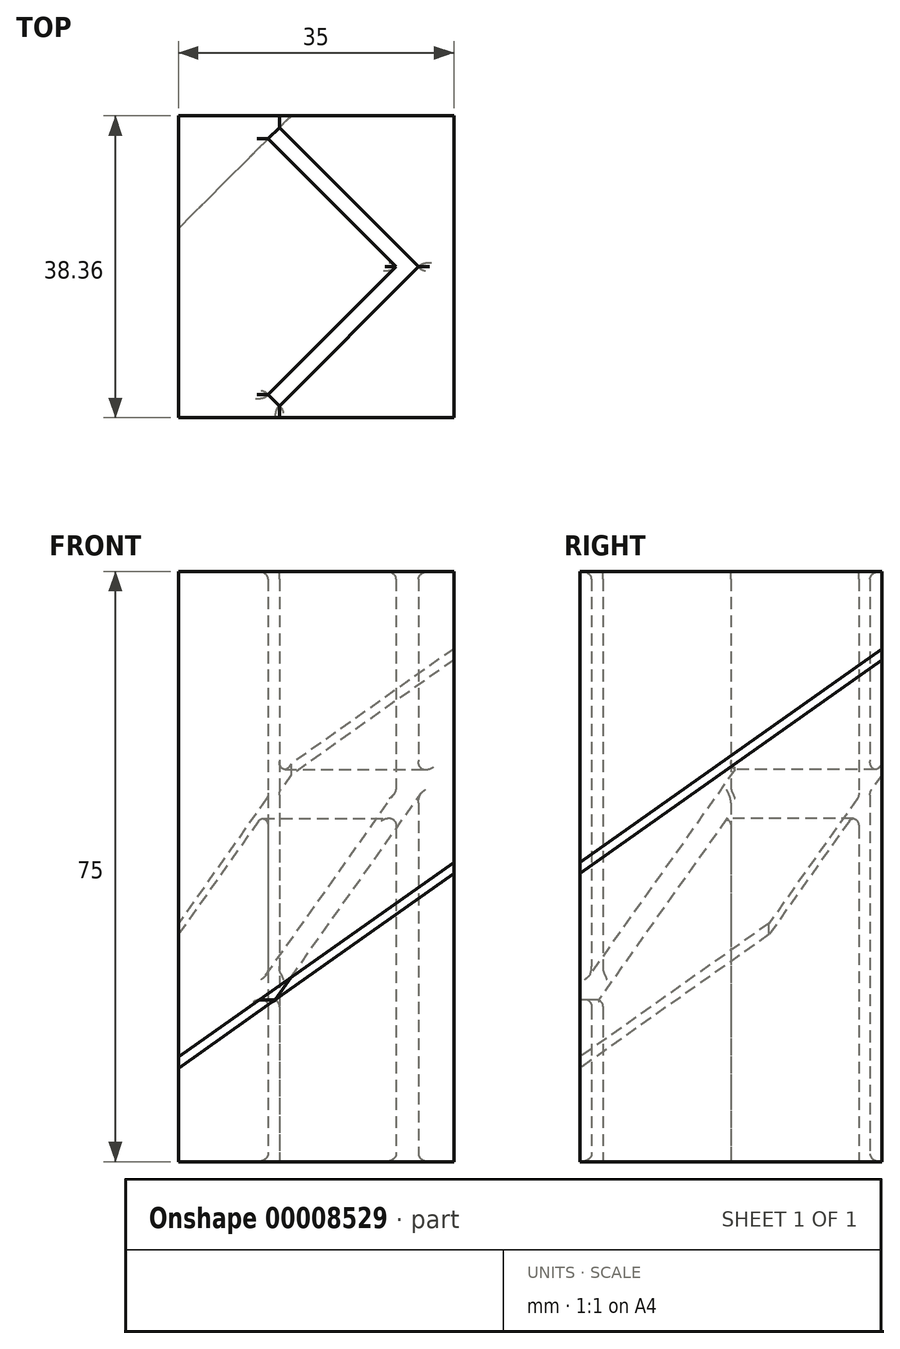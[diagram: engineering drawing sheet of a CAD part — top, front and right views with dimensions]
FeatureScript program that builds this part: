
annotation { "Feature Type Name" : "Feature", "Feature Type Description" : "" }
export const myFeature = defineFeature(function(context is Context, id is Id, definition is map)
    precondition{}
    {
        {
            var Q0;
            Q0=qCreatedBy(makeId("Top.planeOp"),FACE);
            var sketch = newSketch(context, id + "F0", { "sketchPlane" : qUnion([Q0])});
            skLineSegment(sketch, "E0.bottom", {"start": v(-17.5, -19.18) * mm, "end": v(17.5, -19.18) * mm});
            skLineSegment(sketch, "E0.top", {"start": v(-17.5, 19.18) * mm, "end": v(17.5, 19.18) * mm});
            skLineSegment(sketch, "E0.left", {"start": v(-17.5, -19.18) * mm, "end": v(-17.5, 19.18) * mm});
            skLineSegment(sketch, "E0.right", {"start": v(17.5, -19.18) * mm, "end": v(17.5, 19.18) * mm});
            skPoint(sketch, "E0.middle", {"position": v(0, 0) * mm});
            skLineSegment(sketch, "E1.bottom", {"start": v(-22.36, 0) * mm, "end": v(-4.68, -17.68) * mm});
            skLineSegment(sketch, "E1.top", {"start": v(-4.68, 17.68) * mm, "end": v(13, 0) * mm});
            skLineSegment(sketch, "E1.left", {"start": v(-22.36, 0) * mm, "end": v(-4.68, 17.68) * mm});
            skLineSegment(sketch, "E1.right", {"start": v(-4.68, -17.68) * mm, "end": v(13, 0) * mm});
            skLineSegment(sketch, "E2.0", {"start": v(-6.1, -16.26) * mm, "end": v(10.17, 0) * mm});
            skLineSegment(sketch, "E2.1", {"start": v(-6.1, 16.26) * mm, "end": v(10.17, 0) * mm});
            skSolve(sketch);
        }
        {
            var Q0;
            {var subQ9=sQuery(id+"F0.wireOp",EDGE,"E0.bottom");Q0=makeQuery(id+"F0.imprint","IMPRINT",FACE,{"disambiguationData":[TD([[makeQuery(id+"F0.imprint","IMPRINT",EDGE,{"derivedFrom":subQ9}),1.0]])]});}
            var Q1;
            {var subQ0=sQuery(id+"F0.wireOp",EDGE,"E2.0");Q1=makeQuery(id+"F0.imprint","IMPRINT",FACE,{"disambiguationData":[TD([[makeQuery(id+"F0.imprint","IMPRINT",EDGE,{"derivedFrom":subQ0}),1.0]])]});}
            extrude(context, id + "F1", {"entities" : qUnion([Q0, Q1]), "depth" : 75 * mm});
        }
        {
            var Q0;
            Q0=makeQuery(id+"F1.opExtrude","SWEPT_FACE",FACE,{"disambiguationData":[OSD([sQuery(id+"F0.wireOp",EDGE,"E2.0")])]});
            var sketch = newSketch(context, id + "F2", { "sketchPlane" : qUnion([Q0])});
            skLineSegment(sketch, "E3.0.0", {"start": v(-15.8, 0) * mm, "end": v(7.2, 0) * mm});
            skLineSegment(sketch, "E3.0.1", {"start": v(7.2, 0) * mm, "end": v(7.2, 75) * mm});
            skLineSegment(sketch, "E3.0.2", {"start": v(7.2, 75) * mm, "end": v(-15.8, 75) * mm});
            skLineSegment(sketch, "E3.0.3", {"start": v(-15.8, 75) * mm, "end": v(-15.8, 0) * mm});
            skLineSegment(sketch, "E4.0.0", {"start": v(9.2, 0) * mm, "end": v(-15.8, 0) * mm});
            skLineSegment(sketch, "E4.0.1", {"start": v(-15.8, 0) * mm, "end": v(-15.8, 75) * mm});
            skLineSegment(sketch, "E4.0.2", {"start": v(-15.8, 75) * mm, "end": v(9.2, 75) * mm});
            skLineSegment(sketch, "E4.0.3", {"start": v(9.2, 75) * mm, "end": v(9.2, 0) * mm});
            skLineSegment(sketch, "E5", {"start": v(32.72, 70.52) * mm, "end": v(-42.6, -4.8) * mm});
            skLineSegment(sketch, "E6.0", {"start": v(34.67, 73.89) * mm, "end": v(-43.44, -4.23) * mm});
            skLineSegment(sketch, "E7", {"start": v(34.67, 73.89) * mm, "end": v(32.72, 70.52) * mm});
            skLineSegment(sketch, "E8", {"start": v(-42.6, -4.8) * mm, "end": v(-43.44, -4.23) * mm});
            skSolve(sketch);
        }
        {
            var Q0;
            {var subQ0=sQuery(id+"F2.wireOp",EDGE,"E6.0");var subQ1=sQuery(id+"F2.wireOp",EDGE,"E3.0.1");var subQ2=makeQuery(id+"F2.imprint","INTERSECT",VERTEX,{"derivedFrom":[subQ1,subQ0]});Q0=makeQuery(id+"F2.imprint","IMPRINT",FACE,{"disambiguationData":[TD([[makeQuery(id+"F2.imprint","IMPRINT",EDGE,{"disambiguationData":[TD([[subQ2,-1.0]])],"derivedFrom":subQ1}),-1.0]])]});}
            var Q1;
            {var subQ0=sQuery(id+"F2.wireOp",EDGE,"E6.0");var subQ1=sQuery(id+"F2.wireOp",EDGE,"E3.0.1");var subQ2=makeQuery(id+"F2.imprint","INTERSECT",VERTEX,{"derivedFrom":[subQ1,subQ0]});Q1=makeQuery(id+"F2.imprint","IMPRINT",FACE,{"disambiguationData":[TD([[makeQuery(id+"F2.imprint","IMPRINT",EDGE,{"disambiguationData":[TD([[subQ2,-1.0]])],"derivedFrom":subQ1}),1.0]])]});}
            var Q2;
            {var subQ5=sQuery(id+"F2.wireOp",EDGE,"E8");Q2=makeQuery(id+"F2.imprint","IMPRINT",FACE,{"disambiguationData":[TD([[makeQuery(id+"F2.imprint","IMPRINT",EDGE,{"derivedFrom":subQ5}),-1.0]])]});}
            var Q3;
            {var subQ5=sQuery(id+"F2.wireOp",EDGE,"E7");Q3=makeQuery(id+"F2.imprint","IMPRINT",FACE,{"disambiguationData":[TD([[makeQuery(id+"F2.imprint","IMPRINT",EDGE,{"derivedFrom":subQ5}),-1.0]])]});}
            extrude(context, id + "F3", {"entities" : qUnion([Q0, Q1, Q2, Q3]), "operationType" : NewBodyOperationType.REMOVE, "depth" : 46 * mm, "symmetric" : true});
        }
        {
            var Q0;
            Q0=makeQuery(id+"F1.opExtrude","CAP_EDGE",EDGE,{"disambiguationData":[OSD([sQuery(id+"F0.wireOp",EDGE,"E2.0")])],"isStart":false});
            var Q1;
            Q1=makeQuery(id+"F1.opExtrude","CAP_EDGE",EDGE,{"disambiguationData":[OSD([sQuery(id+"F0.wireOp",EDGE,"E2.1")])],"isStart":false});
            var Q2;
            Q2=makeQuery(id+"F1.opExtrude","CAP_EDGE",EDGE,{"disambiguationData":[OSD([sQuery(id+"F0.wireOp",EDGE,"E1.top")])],"isStart":false});
            var Q3;
            Q3=makeQuery(id+"F1.opExtrude","CAP_EDGE",EDGE,{"disambiguationData":[OSD([sQuery(id+"F0.wireOp",EDGE,"E1.right")])],"isStart":false});
            var Q4;
            Q4=makeQuery(id+"F1.opExtrude","CAP_EDGE",EDGE,{"disambiguationData":[OSD([sQuery(id+"F0.wireOp",EDGE,"E1.left")])],"isStart":false});
            var Q5;
            Q5=makeQuery(id+"F1.opExtrude","CAP_EDGE",EDGE,{"disambiguationData":[OSD([sQuery(id+"F0.wireOp",EDGE,"E1.bottom")])],"isStart":false});
            var Q6;
            Q6=makeQuery(id+"F1.opExtrude","CAP_EDGE",EDGE,{"disambiguationData":[OSD([sQuery(id+"F0.wireOp",EDGE,"E1.right")])],"isStart":true});
            var Q7;
            Q7=makeQuery(id+"F1.opExtrude","CAP_EDGE",EDGE,{"disambiguationData":[OSD([sQuery(id+"F0.wireOp",EDGE,"E1.top")])],"isStart":true});
            var Q8;
            Q8=makeQuery(id+"F1.opExtrude","CAP_EDGE",EDGE,{"disambiguationData":[OSD([sQuery(id+"F0.wireOp",EDGE,"E2.1")])],"isStart":true});
            var Q9;
            Q9=makeQuery(id+"F1.opExtrude","CAP_EDGE",EDGE,{"disambiguationData":[OSD([sQuery(id+"F0.wireOp",EDGE,"E2.0")])],"isStart":true});
            var Q10;
            Q10=makeQuery(id+"F1.opExtrude","CAP_EDGE",EDGE,{"disambiguationData":[OSD([sQuery(id+"F0.wireOp",EDGE,"E1.bottom")])],"isStart":true});
            var Q11;
            Q11=makeQuery(id+"F1.opExtrude","CAP_EDGE",EDGE,{"disambiguationData":[OSD([sQuery(id+"F0.wireOp",EDGE,"E1.left")])],"isStart":true});
            var Q12;
            Q12=makeQuery(id+"F3.boolean.opBoolean","INTERSECT",EDGE,{"derivedFrom":[makeQuery(id+"F1.opExtrude","SWEPT_FACE",FACE,{"disambiguationData":[OSD([sQuery(id+"F0.wireOp",EDGE,"E1.top")])]}),makeQuery(id+"F3.opExtrude","SWEPT_FACE",FACE,{"disambiguationData":[OSD([sQuery(id+"F2.wireOp",EDGE,"E5")])]})]});
            var Q13;
            Q13=makeQuery(id+"F3.boolean.opBoolean","INTERSECT",EDGE,{"derivedFrom":[makeQuery(id+"F1.opExtrude","SWEPT_FACE",FACE,{"disambiguationData":[OSD([sQuery(id+"F0.wireOp",EDGE,"E2.1")])]}),makeQuery(id+"F3.opExtrude","SWEPT_FACE",FACE,{"disambiguationData":[OSD([sQuery(id+"F2.wireOp",EDGE,"E5")])]})]});
            var Q14;
            Q14=makeQuery(id+"F3.boolean.opBoolean","INTERSECT",EDGE,{"derivedFrom":[makeQuery(id+"F1.opExtrude","SWEPT_FACE",FACE,{"disambiguationData":[OSD([sQuery(id+"F0.wireOp",EDGE,"E2.0")])]}),makeQuery(id+"F3.opExtrude","SWEPT_FACE",FACE,{"disambiguationData":[OSD([sQuery(id+"F2.wireOp",EDGE,"E5")])]})]});
            var Q15;
            Q15=makeQuery(id+"F3.boolean.opBoolean","INTERSECT",EDGE,{"derivedFrom":[makeQuery(id+"F1.opExtrude","SWEPT_FACE",FACE,{"disambiguationData":[OSD([sQuery(id+"F0.wireOp",EDGE,"E1.right")])]}),makeQuery(id+"F3.opExtrude","SWEPT_FACE",FACE,{"disambiguationData":[OSD([sQuery(id+"F2.wireOp",EDGE,"E5")])]})]});
            var Q16;
            Q16=makeQuery(id+"F3.boolean.opBoolean","INTERSECT",EDGE,{"derivedFrom":[makeQuery(id+"F1.opExtrude","SWEPT_FACE",FACE,{"disambiguationData":[OSD([sQuery(id+"F0.wireOp",EDGE,"E1.bottom")])]}),makeQuery(id+"F3.opExtrude","SWEPT_FACE",FACE,{"disambiguationData":[OSD([sQuery(id+"F2.wireOp",EDGE,"E5")])]})]});
            var Q17;
            Q17=makeQuery(id+"F3.boolean.opBoolean","INTERSECT",EDGE,{"derivedFrom":[makeQuery(id+"F1.opExtrude","SWEPT_FACE",FACE,{"disambiguationData":[OSD([sQuery(id+"F0.wireOp",EDGE,"E2.0")])]}),makeQuery(id+"F3.opExtrude","SWEPT_FACE",FACE,{"disambiguationData":[OSD([sQuery(id+"F2.wireOp",EDGE,"E6.0")])]})]});
            var Q18;
            Q18=makeQuery(id+"F3.boolean.opBoolean","INTERSECT",EDGE,{"derivedFrom":[makeQuery(id+"F1.opExtrude","SWEPT_FACE",FACE,{"disambiguationData":[OSD([sQuery(id+"F0.wireOp",EDGE,"E1.bottom")])]}),makeQuery(id+"F3.opExtrude","SWEPT_FACE",FACE,{"disambiguationData":[OSD([sQuery(id+"F2.wireOp",EDGE,"E6.0")])]})]});
            var Q19;
            Q19=makeQuery(id+"F3.boolean.opBoolean","INTERSECT",EDGE,{"derivedFrom":[makeQuery(id+"F1.opExtrude","SWEPT_FACE",FACE,{"disambiguationData":[OSD([sQuery(id+"F0.wireOp",EDGE,"E1.right")])]}),makeQuery(id+"F3.opExtrude","SWEPT_FACE",FACE,{"disambiguationData":[OSD([sQuery(id+"F2.wireOp",EDGE,"E6.0")])]})]});
            var Q20;
            Q20=makeQuery(id+"F3.boolean.opBoolean","INTERSECT",EDGE,{"derivedFrom":[makeQuery(id+"F1.opExtrude","SWEPT_FACE",FACE,{"disambiguationData":[OSD([sQuery(id+"F0.wireOp",EDGE,"E1.top")])]}),makeQuery(id+"F3.opExtrude","SWEPT_FACE",FACE,{"disambiguationData":[OSD([sQuery(id+"F2.wireOp",EDGE,"E6.0")])]})]});
            var Q21;
            Q21=makeQuery(id+"F3.boolean.opBoolean","INTERSECT",EDGE,{"derivedFrom":[makeQuery(id+"F1.opExtrude","SWEPT_FACE",FACE,{"disambiguationData":[OSD([sQuery(id+"F0.wireOp",EDGE,"E2.1")])]}),makeQuery(id+"F3.opExtrude","SWEPT_FACE",FACE,{"disambiguationData":[OSD([sQuery(id+"F2.wireOp",EDGE,"E6.0")])]})]});
            fillet(context, id + "F4", {"entities" : qUnion([Q0, Q1, Q2, Q3, Q4, Q5, Q6, Q7, Q8, Q9, Q10, Q11, Q12, Q13, Q14, Q15, Q16, Q17, Q18, Q19, Q20, Q21]), "radius" : 1 * mm, "tangentPropagation" : true, "allowEdgeOverflow" : false});
        }
    });
